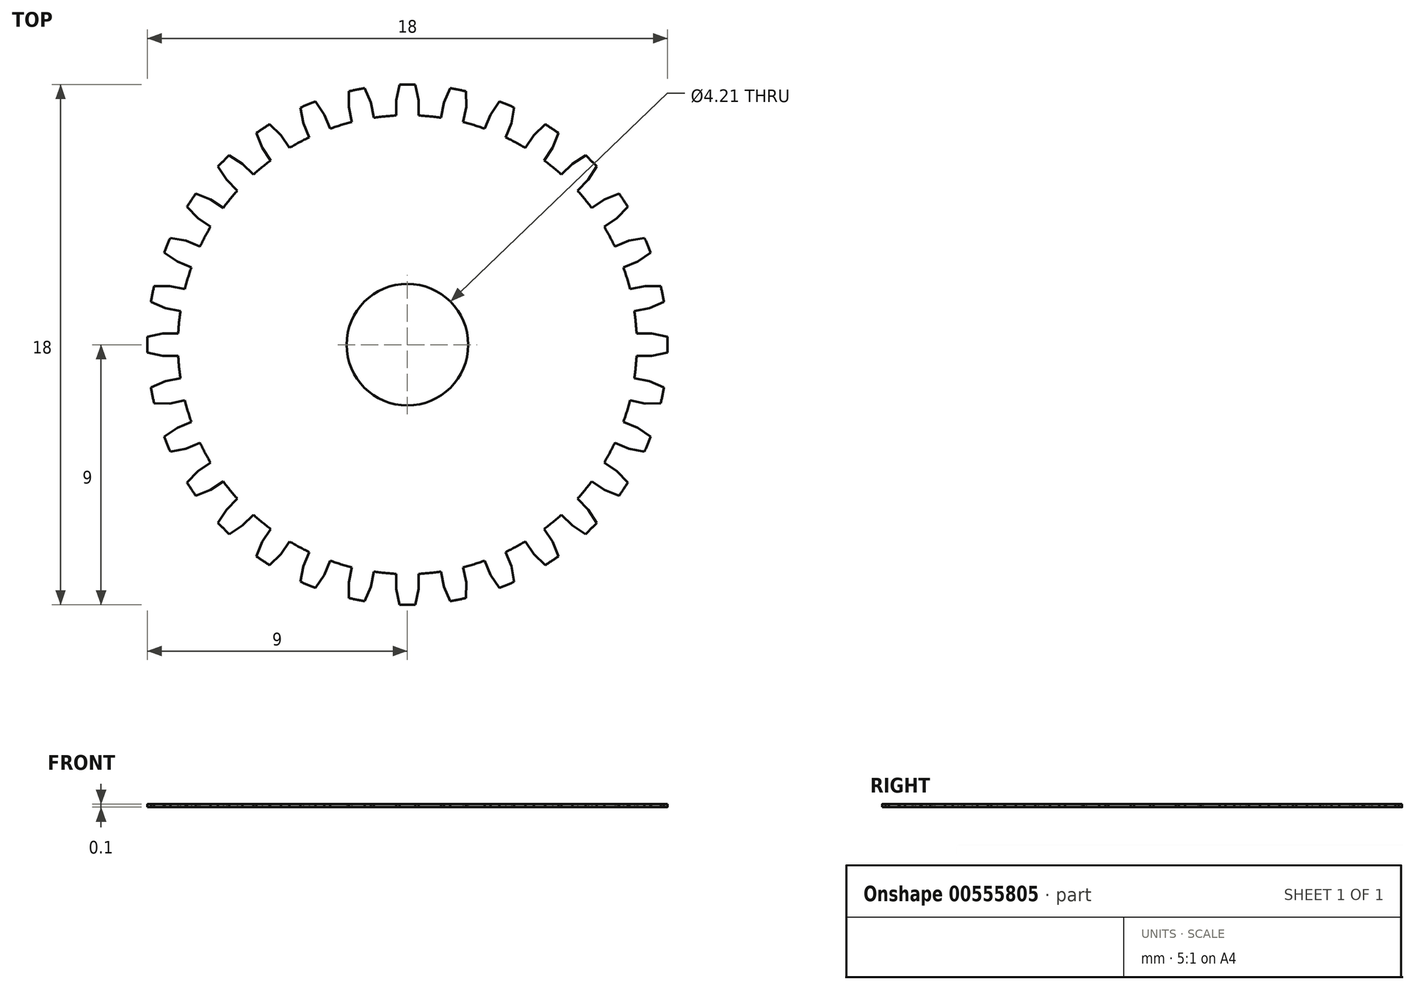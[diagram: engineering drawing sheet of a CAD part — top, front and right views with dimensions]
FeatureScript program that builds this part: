
annotation { "Feature Type Name" : "Feature", "Feature Type Description" : "" }
export const myFeature = defineFeature(function(context is Context, id is Id, definition is map)
    precondition{}
    {
        {
            var Q0;
            Q0=qCreatedBy(makeId("Top.planeOp"),FACE);
            var sketch = newSketch(context, id + "F0", { "sketchPlane" : qUnion([Q0])});
            skCircle(sketch, "E0", {"center": v(0, 0) * mm, "radius": 1.9 * mm});
            skCircle(sketch, "E1.0", {"center": v(0, 0) * mm, "radius": 2.1 * mm});
            skCircle(sketch, "E2", {"center": v(0, 0) * mm, "radius": 8.47 * mm});
            skCircle(sketch, "E3", {"center": v(0, 0) * mm, "radius": 9 * mm});
            skCircle(sketch, "E4", {"center": v(0, 0) * mm, "radius": 7.94 * mm});
            skLineSegment(sketch, "E5", {"start": v(0, 0) * mm, "end": v(0, 9) * mm});
            skLineSegment(sketch, "E6", {"start": v(0, 0) * mm, "end": v(0.88, 8.95) * mm});
            skPoint(sketch, "E7", {"position": v(0.39, 7.93) * mm});
            skPoint(sketch, "E8", {"position": v(0.28, 9) * mm});
            skPoint(sketch, "E9", {"position": v(0.39, 8.46) * mm});
            skArc(sketch, "E10", {"start": v(0.39, 7.93) * mm, "mid": v(0.58, 7.92) * mm, "end": v(0.78, 7.9) * mm});
            skArc(sketch, "E11", {"start": v(0, 9) * mm, "mid": v(0.14, 9) * mm, "end": v(0.28, 9) * mm});
            skLineSegment(sketch, "E12", {"start": v(0.28, 9) * mm, "end": v(0.39, 8.46) * mm});
            skLineSegment(sketch, "E13", {"start": v(0.39, 7.93) * mm, "end": v(0.39, 8.46) * mm});
            skArc(sketch, "E14.MirrorCS", {"start": v(0, 9) * mm, "mid": v(-0.14, 9) * mm, "end": v(-0.28, 9) * mm});
            skPoint(sketch, "E15.MirrorP", {"position": v(-0.39, 8.46) * mm});
            skPoint(sketch, "E16.MirrorP", {"position": v(-0.39, 7.93) * mm});
            skPoint(sketch, "E17.MirrorP", {"position": v(-0.28, 9) * mm});
            skArc(sketch, "E18.MirrorCS", {"start": v(-0.39, 7.93) * mm, "mid": v(-0.58, 7.92) * mm, "end": v(-0.78, 7.9) * mm});
            skLineSegment(sketch, "E19.MirrorCS", {"start": v(-0.39, 7.93) * mm, "end": v(-0.39, 8.46) * mm});
            skLineSegment(sketch, "E20.MirrorCS", {"start": v(-0.28, 9) * mm, "end": v(-0.39, 8.46) * mm});
            skPoint(sketch, "E21.1.0", {"position": v(-2.03, 8.22) * mm});
            skPoint(sketch, "E21.1.1", {"position": v(-2.02, 8.76) * mm});
            skPoint(sketch, "E21.1.2", {"position": v(-1.93, 7.7) * mm});
            skArc(sketch, "E21.1.3", {"start": v(-1.16, 7.85) * mm, "mid": v(-0.97, 7.88) * mm, "end": v(-0.78, 7.9) * mm});
            skLineSegment(sketch, "E21.1.4", {"start": v(-1.48, 8.87) * mm, "end": v(-1.27, 8.37) * mm});
            skLineSegment(sketch, "E21.1.5", {"start": v(-1.16, 7.85) * mm, "end": v(-1.27, 8.37) * mm});
            skArc(sketch, "E21.1.6", {"start": v(-1.93, 7.7) * mm, "mid": v(-2.12, 7.65) * mm, "end": v(-2.3, 7.6) * mm});
            skPoint(sketch, "E21.1.7", {"position": v(-1.27, 8.37) * mm});
            skPoint(sketch, "E21.1.8", {"position": v(-1.48, 8.87) * mm});
            skPoint(sketch, "E21.1.9", {"position": v(-1.16, 7.85) * mm});
            skLineSegment(sketch, "E21.1.10", {"start": v(-1.93, 7.7) * mm, "end": v(-2.03, 8.22) * mm});
            skLineSegment(sketch, "E21.1.11", {"start": v(-2.02, 8.76) * mm, "end": v(-2.03, 8.22) * mm});
            skArc(sketch, "E21.1.12", {"start": v(-1.76, 8.82) * mm, "mid": v(-1.62, 8.85) * mm, "end": v(-1.48, 8.87) * mm});
            skArc(sketch, "E21.1.13", {"start": v(-1.76, 8.82) * mm, "mid": v(-1.9, 8.8) * mm, "end": v(-2.02, 8.76) * mm});
            skPoint(sketch, "E21.2.0", {"position": v(-3.6, 7.66) * mm});
            skPoint(sketch, "E21.2.1", {"position": v(-3.7, 8.2) * mm});
            skPoint(sketch, "E21.2.2", {"position": v(-3.4, 7.18) * mm});
            skArc(sketch, "E21.2.3", {"start": v(-2.67, 7.47) * mm, "mid": v(-2.49, 7.54) * mm, "end": v(-2.3, 7.6) * mm});
            skLineSegment(sketch, "E21.2.4", {"start": v(-3.19, 8.41) * mm, "end": v(-2.88, 7.96) * mm});
            skLineSegment(sketch, "E21.2.5", {"start": v(-2.67, 7.47) * mm, "end": v(-2.88, 7.96) * mm});
            skArc(sketch, "E21.2.6", {"start": v(-3.4, 7.18) * mm, "mid": v(-3.57, 7.09) * mm, "end": v(-3.74, 7) * mm});
            skPoint(sketch, "E21.2.7", {"position": v(-2.88, 7.96) * mm});
            skPoint(sketch, "E21.2.8", {"position": v(-3.19, 8.41) * mm});
            skPoint(sketch, "E21.2.9", {"position": v(-2.67, 7.47) * mm});
            skLineSegment(sketch, "E21.2.10", {"start": v(-3.4, 7.18) * mm, "end": v(-3.6, 7.66) * mm});
            skLineSegment(sketch, "E21.2.11", {"start": v(-3.7, 8.2) * mm, "end": v(-3.6, 7.66) * mm});
            skArc(sketch, "E21.2.12", {"start": v(-3.44, 8.31) * mm, "mid": v(-3.31, 8.36) * mm, "end": v(-3.19, 8.41) * mm});
            skArc(sketch, "E21.2.13", {"start": v(-3.44, 8.31) * mm, "mid": v(-3.57, 8.26) * mm, "end": v(-3.7, 8.2) * mm});
            skPoint(sketch, "E21.3.0", {"position": v(-5.02, 6.82) * mm});
            skPoint(sketch, "E21.3.1", {"position": v(-5.22, 7.32) * mm});
            skPoint(sketch, "E21.3.2", {"position": v(-4.73, 6.38) * mm});
            skArc(sketch, "E21.3.3", {"start": v(-4.08, 6.8) * mm, "mid": v(-3.91, 6.9) * mm, "end": v(-3.74, 7) * mm});
            skLineSegment(sketch, "E21.3.4", {"start": v(-4.77, 7.63) * mm, "end": v(-4.37, 7.25) * mm});
            skLineSegment(sketch, "E21.3.5", {"start": v(-4.08, 6.8) * mm, "end": v(-4.37, 7.25) * mm});
            skArc(sketch, "E21.3.6", {"start": v(-4.73, 6.38) * mm, "mid": v(-4.88, 6.26) * mm, "end": v(-5.04, 6.14) * mm});
            skPoint(sketch, "E21.3.7", {"position": v(-4.37, 7.25) * mm});
            skPoint(sketch, "E21.3.8", {"position": v(-4.77, 7.63) * mm});
            skPoint(sketch, "E21.3.9", {"position": v(-4.08, 6.8) * mm});
            skLineSegment(sketch, "E21.3.10", {"start": v(-4.73, 6.38) * mm, "end": v(-5.02, 6.82) * mm});
            skLineSegment(sketch, "E21.3.11", {"start": v(-5.22, 7.32) * mm, "end": v(-5.02, 6.82) * mm});
            skArc(sketch, "E21.3.12", {"start": v(-5, 7.48) * mm, "mid": v(-4.88, 7.56) * mm, "end": v(-4.77, 7.63) * mm});
            skArc(sketch, "E21.3.13", {"start": v(-5, 7.48) * mm, "mid": v(-5.11, 7.4) * mm, "end": v(-5.22, 7.32) * mm});
            skPoint(sketch, "E21.4.0", {"position": v(-6.26, 5.7) * mm});
            skPoint(sketch, "E21.4.1", {"position": v(-6.55, 6.16) * mm});
            skPoint(sketch, "E21.4.2", {"position": v(-5.88, 5.33) * mm});
            skArc(sketch, "E21.4.3", {"start": v(-5.33, 5.88) * mm, "mid": v(-5.18, 6.01) * mm, "end": v(-5.04, 6.14) * mm});
            skLineSegment(sketch, "E21.4.4", {"start": v(-6.16, 6.55) * mm, "end": v(-5.7, 6.26) * mm});
            skLineSegment(sketch, "E21.4.5", {"start": v(-5.33, 5.88) * mm, "end": v(-5.7, 6.26) * mm});
            skArc(sketch, "E21.4.6", {"start": v(-5.88, 5.33) * mm, "mid": v(-6.01, 5.18) * mm, "end": v(-6.14, 5.04) * mm});
            skPoint(sketch, "E21.4.7", {"position": v(-5.7, 6.26) * mm});
            skPoint(sketch, "E21.4.8", {"position": v(-6.16, 6.55) * mm});
            skPoint(sketch, "E21.4.9", {"position": v(-5.33, 5.88) * mm});
            skLineSegment(sketch, "E21.4.10", {"start": v(-5.88, 5.33) * mm, "end": v(-6.26, 5.7) * mm});
            skLineSegment(sketch, "E21.4.11", {"start": v(-6.55, 6.16) * mm, "end": v(-6.26, 5.7) * mm});
            skArc(sketch, "E21.4.12", {"start": v(-6.36, 6.36) * mm, "mid": v(-6.26, 6.46) * mm, "end": v(-6.16, 6.55) * mm});
            skArc(sketch, "E21.4.13", {"start": v(-6.36, 6.36) * mm, "mid": v(-6.46, 6.26) * mm, "end": v(-6.55, 6.16) * mm});
            skPoint(sketch, "E21.5.0", {"position": v(-7.25, 4.37) * mm});
            skPoint(sketch, "E21.5.1", {"position": v(-7.63, 4.77) * mm});
            skPoint(sketch, "E21.5.2", {"position": v(-6.8, 4.08) * mm});
            skArc(sketch, "E21.5.3", {"start": v(-6.38, 4.73) * mm, "mid": v(-6.26, 4.88) * mm, "end": v(-6.14, 5.04) * mm});
            skLineSegment(sketch, "E21.5.4", {"start": v(-7.32, 5.22) * mm, "end": v(-6.82, 5.02) * mm});
            skLineSegment(sketch, "E21.5.5", {"start": v(-6.38, 4.73) * mm, "end": v(-6.82, 5.02) * mm});
            skArc(sketch, "E21.5.6", {"start": v(-6.8, 4.08) * mm, "mid": v(-6.9, 3.91) * mm, "end": v(-7, 3.74) * mm});
            skPoint(sketch, "E21.5.7", {"position": v(-6.82, 5.02) * mm});
            skPoint(sketch, "E21.5.8", {"position": v(-7.32, 5.22) * mm});
            skPoint(sketch, "E21.5.9", {"position": v(-6.38, 4.73) * mm});
            skLineSegment(sketch, "E21.5.10", {"start": v(-6.8, 4.08) * mm, "end": v(-7.25, 4.37) * mm});
            skLineSegment(sketch, "E21.5.11", {"start": v(-7.63, 4.77) * mm, "end": v(-7.25, 4.37) * mm});
            skArc(sketch, "E21.5.12", {"start": v(-7.48, 5) * mm, "mid": v(-7.4, 5.11) * mm, "end": v(-7.32, 5.22) * mm});
            skArc(sketch, "E21.5.13", {"start": v(-7.48, 5) * mm, "mid": v(-7.56, 4.88) * mm, "end": v(-7.63, 4.77) * mm});
            skPoint(sketch, "E21.6.0", {"position": v(-7.96, 2.88) * mm});
            skPoint(sketch, "E21.6.1", {"position": v(-8.41, 3.19) * mm});
            skPoint(sketch, "E21.6.2", {"position": v(-7.47, 2.67) * mm});
            skArc(sketch, "E21.6.3", {"start": v(-7.18, 3.4) * mm, "mid": v(-7.09, 3.57) * mm, "end": v(-7, 3.74) * mm});
            skLineSegment(sketch, "E21.6.4", {"start": v(-8.2, 3.7) * mm, "end": v(-7.66, 3.6) * mm});
            skLineSegment(sketch, "E21.6.5", {"start": v(-7.18, 3.4) * mm, "end": v(-7.66, 3.6) * mm});
            skArc(sketch, "E21.6.6", {"start": v(-7.47, 2.67) * mm, "mid": v(-7.54, 2.49) * mm, "end": v(-7.6, 2.3) * mm});
            skPoint(sketch, "E21.6.7", {"position": v(-7.66, 3.6) * mm});
            skPoint(sketch, "E21.6.8", {"position": v(-8.2, 3.7) * mm});
            skPoint(sketch, "E21.6.9", {"position": v(-7.18, 3.4) * mm});
            skLineSegment(sketch, "E21.6.10", {"start": v(-7.47, 2.67) * mm, "end": v(-7.96, 2.88) * mm});
            skLineSegment(sketch, "E21.6.11", {"start": v(-8.41, 3.19) * mm, "end": v(-7.96, 2.88) * mm});
            skArc(sketch, "E21.6.12", {"start": v(-8.31, 3.44) * mm, "mid": v(-8.26, 3.57) * mm, "end": v(-8.2, 3.7) * mm});
            skArc(sketch, "E21.6.13", {"start": v(-8.31, 3.44) * mm, "mid": v(-8.36, 3.31) * mm, "end": v(-8.41, 3.19) * mm});
            skPoint(sketch, "E21.7.0", {"position": v(-8.37, 1.27) * mm});
            skPoint(sketch, "E21.7.1", {"position": v(-8.87, 1.48) * mm});
            skPoint(sketch, "E21.7.2", {"position": v(-7.85, 1.16) * mm});
            skArc(sketch, "E21.7.3", {"start": v(-7.7, 1.93) * mm, "mid": v(-7.65, 2.12) * mm, "end": v(-7.6, 2.3) * mm});
            skLineSegment(sketch, "E21.7.4", {"start": v(-8.76, 2.02) * mm, "end": v(-8.22, 2.03) * mm});
            skLineSegment(sketch, "E21.7.5", {"start": v(-7.7, 1.93) * mm, "end": v(-8.22, 2.03) * mm});
            skArc(sketch, "E21.7.6", {"start": v(-7.85, 1.16) * mm, "mid": v(-7.88, 0.97) * mm, "end": v(-7.9, 0.78) * mm});
            skPoint(sketch, "E21.7.7", {"position": v(-8.22, 2.03) * mm});
            skPoint(sketch, "E21.7.8", {"position": v(-8.76, 2.02) * mm});
            skPoint(sketch, "E21.7.9", {"position": v(-7.7, 1.93) * mm});
            skLineSegment(sketch, "E21.7.10", {"start": v(-7.85, 1.16) * mm, "end": v(-8.37, 1.27) * mm});
            skLineSegment(sketch, "E21.7.11", {"start": v(-8.87, 1.48) * mm, "end": v(-8.37, 1.27) * mm});
            skArc(sketch, "E21.7.12", {"start": v(-8.82, 1.76) * mm, "mid": v(-8.8, 1.9) * mm, "end": v(-8.76, 2.02) * mm});
            skArc(sketch, "E21.7.13", {"start": v(-8.82, 1.76) * mm, "mid": v(-8.85, 1.62) * mm, "end": v(-8.87, 1.48) * mm});
            skPoint(sketch, "E21.8.0", {"position": v(-8.46, -0.39) * mm});
            skPoint(sketch, "E21.8.1", {"position": v(-9, -0.28) * mm});
            skPoint(sketch, "E21.8.2", {"position": v(-7.93, -0.39) * mm});
            skArc(sketch, "E21.8.3", {"start": v(-7.93, 0.39) * mm, "mid": v(-7.92, 0.58) * mm, "end": v(-7.9, 0.78) * mm});
            skLineSegment(sketch, "E21.8.4", {"start": v(-9, 0.28) * mm, "end": v(-8.46, 0.39) * mm});
            skLineSegment(sketch, "E21.8.5", {"start": v(-7.93, 0.39) * mm, "end": v(-8.46, 0.39) * mm});
            skArc(sketch, "E21.8.6", {"start": v(-7.93, -0.39) * mm, "mid": v(-7.92, -0.58) * mm, "end": v(-7.9, -0.78) * mm});
            skPoint(sketch, "E21.8.7", {"position": v(-8.46, 0.39) * mm});
            skPoint(sketch, "E21.8.8", {"position": v(-9, 0.28) * mm});
            skPoint(sketch, "E21.8.9", {"position": v(-7.93, 0.39) * mm});
            skLineSegment(sketch, "E21.8.10", {"start": v(-7.93, -0.39) * mm, "end": v(-8.46, -0.39) * mm});
            skLineSegment(sketch, "E21.8.11", {"start": v(-9, -0.28) * mm, "end": v(-8.46, -0.39) * mm});
            skArc(sketch, "E21.8.12", {"start": v(-9, 0) * mm, "mid": v(-9, 0.14) * mm, "end": v(-9, 0.28) * mm});
            skArc(sketch, "E21.8.13", {"start": v(-9, 0) * mm, "mid": v(-9, -0.14) * mm, "end": v(-9, -0.28) * mm});
            skPoint(sketch, "E21.9.0", {"position": v(-8.22, -2.03) * mm});
            skPoint(sketch, "E21.9.1", {"position": v(-8.76, -2.02) * mm});
            skPoint(sketch, "E21.9.2", {"position": v(-7.7, -1.93) * mm});
            skArc(sketch, "E21.9.3", {"start": v(-7.85, -1.16) * mm, "mid": v(-7.88, -0.97) * mm, "end": v(-7.9, -0.78) * mm});
            skLineSegment(sketch, "E21.9.4", {"start": v(-8.87, -1.48) * mm, "end": v(-8.37, -1.27) * mm});
            skLineSegment(sketch, "E21.9.5", {"start": v(-7.85, -1.16) * mm, "end": v(-8.37, -1.27) * mm});
            skArc(sketch, "E21.9.6", {"start": v(-7.7, -1.93) * mm, "mid": v(-7.65, -2.12) * mm, "end": v(-7.6, -2.3) * mm});
            skPoint(sketch, "E21.9.7", {"position": v(-8.37, -1.27) * mm});
            skPoint(sketch, "E21.9.8", {"position": v(-8.87, -1.48) * mm});
            skPoint(sketch, "E21.9.9", {"position": v(-7.85, -1.16) * mm});
            skLineSegment(sketch, "E21.9.10", {"start": v(-7.7, -1.93) * mm, "end": v(-8.22, -2.03) * mm});
            skLineSegment(sketch, "E21.9.11", {"start": v(-8.76, -2.02) * mm, "end": v(-8.22, -2.03) * mm});
            skArc(sketch, "E21.9.12", {"start": v(-8.82, -1.76) * mm, "mid": v(-8.85, -1.62) * mm, "end": v(-8.87, -1.48) * mm});
            skArc(sketch, "E21.9.13", {"start": v(-8.82, -1.76) * mm, "mid": v(-8.8, -1.9) * mm, "end": v(-8.76, -2.02) * mm});
            skPoint(sketch, "E21.10.0", {"position": v(-7.66, -3.6) * mm});
            skPoint(sketch, "E21.10.1", {"position": v(-8.2, -3.7) * mm});
            skPoint(sketch, "E21.10.2", {"position": v(-7.18, -3.4) * mm});
            skArc(sketch, "E21.10.3", {"start": v(-7.47, -2.67) * mm, "mid": v(-7.54, -2.49) * mm, "end": v(-7.6, -2.3) * mm});
            skLineSegment(sketch, "E21.10.4", {"start": v(-8.41, -3.19) * mm, "end": v(-7.96, -2.88) * mm});
            skLineSegment(sketch, "E21.10.5", {"start": v(-7.47, -2.67) * mm, "end": v(-7.96, -2.88) * mm});
            skArc(sketch, "E21.10.6", {"start": v(-7.18, -3.4) * mm, "mid": v(-7.09, -3.57) * mm, "end": v(-7, -3.74) * mm});
            skPoint(sketch, "E21.10.7", {"position": v(-7.96, -2.88) * mm});
            skPoint(sketch, "E21.10.8", {"position": v(-8.41, -3.19) * mm});
            skPoint(sketch, "E21.10.9", {"position": v(-7.47, -2.67) * mm});
            skLineSegment(sketch, "E21.10.10", {"start": v(-7.18, -3.4) * mm, "end": v(-7.66, -3.6) * mm});
            skLineSegment(sketch, "E21.10.11", {"start": v(-8.2, -3.7) * mm, "end": v(-7.66, -3.6) * mm});
            skArc(sketch, "E21.10.12", {"start": v(-8.31, -3.44) * mm, "mid": v(-8.36, -3.31) * mm, "end": v(-8.41, -3.19) * mm});
            skArc(sketch, "E21.10.13", {"start": v(-8.31, -3.44) * mm, "mid": v(-8.26, -3.57) * mm, "end": v(-8.2, -3.7) * mm});
            skPoint(sketch, "E21.11.0", {"position": v(-6.82, -5.02) * mm});
            skPoint(sketch, "E21.11.1", {"position": v(-7.32, -5.22) * mm});
            skPoint(sketch, "E21.11.2", {"position": v(-6.38, -4.73) * mm});
            skArc(sketch, "E21.11.3", {"start": v(-6.8, -4.08) * mm, "mid": v(-6.9, -3.91) * mm, "end": v(-7, -3.74) * mm});
            skLineSegment(sketch, "E21.11.4", {"start": v(-7.63, -4.77) * mm, "end": v(-7.25, -4.37) * mm});
            skLineSegment(sketch, "E21.11.5", {"start": v(-6.8, -4.08) * mm, "end": v(-7.25, -4.37) * mm});
            skArc(sketch, "E21.11.6", {"start": v(-6.38, -4.73) * mm, "mid": v(-6.26, -4.88) * mm, "end": v(-6.14, -5.04) * mm});
            skPoint(sketch, "E21.11.7", {"position": v(-7.25, -4.37) * mm});
            skPoint(sketch, "E21.11.8", {"position": v(-7.63, -4.77) * mm});
            skPoint(sketch, "E21.11.9", {"position": v(-6.8, -4.08) * mm});
            skLineSegment(sketch, "E21.11.10", {"start": v(-6.38, -4.73) * mm, "end": v(-6.82, -5.02) * mm});
            skLineSegment(sketch, "E21.11.11", {"start": v(-7.32, -5.22) * mm, "end": v(-6.82, -5.02) * mm});
            skArc(sketch, "E21.11.12", {"start": v(-7.48, -5) * mm, "mid": v(-7.56, -4.88) * mm, "end": v(-7.63, -4.77) * mm});
            skArc(sketch, "E21.11.13", {"start": v(-7.48, -5) * mm, "mid": v(-7.4, -5.11) * mm, "end": v(-7.32, -5.22) * mm});
            skPoint(sketch, "E21.12.0", {"position": v(-5.7, -6.26) * mm});
            skPoint(sketch, "E21.12.1", {"position": v(-6.16, -6.55) * mm});
            skPoint(sketch, "E21.12.2", {"position": v(-5.33, -5.88) * mm});
            skArc(sketch, "E21.12.3", {"start": v(-5.88, -5.33) * mm, "mid": v(-6.01, -5.18) * mm, "end": v(-6.14, -5.04) * mm});
            skLineSegment(sketch, "E21.12.4", {"start": v(-6.55, -6.16) * mm, "end": v(-6.26, -5.7) * mm});
            skLineSegment(sketch, "E21.12.5", {"start": v(-5.88, -5.33) * mm, "end": v(-6.26, -5.7) * mm});
            skArc(sketch, "E21.12.6", {"start": v(-5.33, -5.88) * mm, "mid": v(-5.18, -6.01) * mm, "end": v(-5.04, -6.14) * mm});
            skPoint(sketch, "E21.12.7", {"position": v(-6.26, -5.7) * mm});
            skPoint(sketch, "E21.12.8", {"position": v(-6.55, -6.16) * mm});
            skPoint(sketch, "E21.12.9", {"position": v(-5.88, -5.33) * mm});
            skLineSegment(sketch, "E21.12.10", {"start": v(-5.33, -5.88) * mm, "end": v(-5.7, -6.26) * mm});
            skLineSegment(sketch, "E21.12.11", {"start": v(-6.16, -6.55) * mm, "end": v(-5.7, -6.26) * mm});
            skArc(sketch, "E21.12.12", {"start": v(-6.36, -6.36) * mm, "mid": v(-6.46, -6.26) * mm, "end": v(-6.55, -6.16) * mm});
            skArc(sketch, "E21.12.13", {"start": v(-6.36, -6.36) * mm, "mid": v(-6.26, -6.46) * mm, "end": v(-6.16, -6.55) * mm});
            skPoint(sketch, "E21.13.0", {"position": v(-4.37, -7.25) * mm});
            skPoint(sketch, "E21.13.1", {"position": v(-4.77, -7.63) * mm});
            skPoint(sketch, "E21.13.2", {"position": v(-4.08, -6.8) * mm});
            skArc(sketch, "E21.13.3", {"start": v(-4.73, -6.38) * mm, "mid": v(-4.88, -6.26) * mm, "end": v(-5.04, -6.14) * mm});
            skLineSegment(sketch, "E21.13.4", {"start": v(-5.22, -7.32) * mm, "end": v(-5.02, -6.82) * mm});
            skLineSegment(sketch, "E21.13.5", {"start": v(-4.73, -6.38) * mm, "end": v(-5.02, -6.82) * mm});
            skArc(sketch, "E21.13.6", {"start": v(-4.08, -6.8) * mm, "mid": v(-3.91, -6.9) * mm, "end": v(-3.74, -7) * mm});
            skPoint(sketch, "E21.13.7", {"position": v(-5.02, -6.82) * mm});
            skPoint(sketch, "E21.13.8", {"position": v(-5.22, -7.32) * mm});
            skPoint(sketch, "E21.13.9", {"position": v(-4.73, -6.38) * mm});
            skLineSegment(sketch, "E21.13.10", {"start": v(-4.08, -6.8) * mm, "end": v(-4.37, -7.25) * mm});
            skLineSegment(sketch, "E21.13.11", {"start": v(-4.77, -7.63) * mm, "end": v(-4.37, -7.25) * mm});
            skArc(sketch, "E21.13.12", {"start": v(-5, -7.48) * mm, "mid": v(-5.11, -7.4) * mm, "end": v(-5.22, -7.32) * mm});
            skArc(sketch, "E21.13.13", {"start": v(-5, -7.48) * mm, "mid": v(-4.88, -7.56) * mm, "end": v(-4.77, -7.63) * mm});
            skPoint(sketch, "E21.14.0", {"position": v(-2.88, -7.96) * mm});
            skPoint(sketch, "E21.14.1", {"position": v(-3.19, -8.41) * mm});
            skPoint(sketch, "E21.14.2", {"position": v(-2.67, -7.47) * mm});
            skArc(sketch, "E21.14.3", {"start": v(-3.4, -7.18) * mm, "mid": v(-3.57, -7.09) * mm, "end": v(-3.74, -7) * mm});
            skLineSegment(sketch, "E21.14.4", {"start": v(-3.7, -8.2) * mm, "end": v(-3.6, -7.66) * mm});
            skLineSegment(sketch, "E21.14.5", {"start": v(-3.4, -7.18) * mm, "end": v(-3.6, -7.66) * mm});
            skArc(sketch, "E21.14.6", {"start": v(-2.67, -7.47) * mm, "mid": v(-2.49, -7.54) * mm, "end": v(-2.3, -7.6) * mm});
            skPoint(sketch, "E21.14.7", {"position": v(-3.6, -7.66) * mm});
            skPoint(sketch, "E21.14.8", {"position": v(-3.7, -8.2) * mm});
            skPoint(sketch, "E21.14.9", {"position": v(-3.4, -7.18) * mm});
            skLineSegment(sketch, "E21.14.10", {"start": v(-2.67, -7.47) * mm, "end": v(-2.88, -7.96) * mm});
            skLineSegment(sketch, "E21.14.11", {"start": v(-3.19, -8.41) * mm, "end": v(-2.88, -7.96) * mm});
            skArc(sketch, "E21.14.12", {"start": v(-3.44, -8.31) * mm, "mid": v(-3.57, -8.26) * mm, "end": v(-3.7, -8.2) * mm});
            skArc(sketch, "E21.14.13", {"start": v(-3.44, -8.31) * mm, "mid": v(-3.31, -8.36) * mm, "end": v(-3.19, -8.41) * mm});
            skPoint(sketch, "E21.15.0", {"position": v(-1.27, -8.37) * mm});
            skPoint(sketch, "E21.15.1", {"position": v(-1.48, -8.87) * mm});
            skPoint(sketch, "E21.15.2", {"position": v(-1.16, -7.85) * mm});
            skArc(sketch, "E21.15.3", {"start": v(-1.93, -7.7) * mm, "mid": v(-2.12, -7.65) * mm, "end": v(-2.3, -7.6) * mm});
            skLineSegment(sketch, "E21.15.4", {"start": v(-2.02, -8.76) * mm, "end": v(-2.03, -8.22) * mm});
            skLineSegment(sketch, "E21.15.5", {"start": v(-1.93, -7.7) * mm, "end": v(-2.03, -8.22) * mm});
            skArc(sketch, "E21.15.6", {"start": v(-1.16, -7.85) * mm, "mid": v(-0.97, -7.88) * mm, "end": v(-0.78, -7.9) * mm});
            skPoint(sketch, "E21.15.7", {"position": v(-2.03, -8.22) * mm});
            skPoint(sketch, "E21.15.8", {"position": v(-2.02, -8.76) * mm});
            skPoint(sketch, "E21.15.9", {"position": v(-1.93, -7.7) * mm});
            skLineSegment(sketch, "E21.15.10", {"start": v(-1.16, -7.85) * mm, "end": v(-1.27, -8.37) * mm});
            skLineSegment(sketch, "E21.15.11", {"start": v(-1.48, -8.87) * mm, "end": v(-1.27, -8.37) * mm});
            skArc(sketch, "E21.15.12", {"start": v(-1.76, -8.82) * mm, "mid": v(-1.9, -8.8) * mm, "end": v(-2.02, -8.76) * mm});
            skArc(sketch, "E21.15.13", {"start": v(-1.76, -8.82) * mm, "mid": v(-1.62, -8.85) * mm, "end": v(-1.48, -8.87) * mm});
            skPoint(sketch, "E21.16.0", {"position": v(0.39, -8.46) * mm});
            skPoint(sketch, "E21.16.1", {"position": v(0.28, -9) * mm});
            skPoint(sketch, "E21.16.2", {"position": v(0.39, -7.93) * mm});
            skArc(sketch, "E21.16.3", {"start": v(-0.39, -7.93) * mm, "mid": v(-0.58, -7.92) * mm, "end": v(-0.78, -7.9) * mm});
            skLineSegment(sketch, "E21.16.4", {"start": v(-0.28, -9) * mm, "end": v(-0.39, -8.46) * mm});
            skLineSegment(sketch, "E21.16.5", {"start": v(-0.39, -7.93) * mm, "end": v(-0.39, -8.46) * mm});
            skArc(sketch, "E21.16.6", {"start": v(0.39, -7.93) * mm, "mid": v(0.58, -7.92) * mm, "end": v(0.78, -7.9) * mm});
            skPoint(sketch, "E21.16.7", {"position": v(-0.39, -8.46) * mm});
            skPoint(sketch, "E21.16.8", {"position": v(-0.28, -9) * mm});
            skPoint(sketch, "E21.16.9", {"position": v(-0.39, -7.93) * mm});
            skLineSegment(sketch, "E21.16.10", {"start": v(0.39, -7.93) * mm, "end": v(0.39, -8.46) * mm});
            skLineSegment(sketch, "E21.16.11", {"start": v(0.28, -9) * mm, "end": v(0.39, -8.46) * mm});
            skArc(sketch, "E21.16.12", {"start": v(0, -9) * mm, "mid": v(-0.14, -9) * mm, "end": v(-0.28, -9) * mm});
            skArc(sketch, "E21.16.13", {"start": v(0, -9) * mm, "mid": v(0.14, -9) * mm, "end": v(0.28, -9) * mm});
            skPoint(sketch, "E21.17.0", {"position": v(2.03, -8.22) * mm});
            skPoint(sketch, "E21.17.1", {"position": v(2.02, -8.76) * mm});
            skPoint(sketch, "E21.17.2", {"position": v(1.93, -7.7) * mm});
            skArc(sketch, "E21.17.3", {"start": v(1.16, -7.85) * mm, "mid": v(0.97, -7.88) * mm, "end": v(0.78, -7.9) * mm});
            skLineSegment(sketch, "E21.17.4", {"start": v(1.48, -8.87) * mm, "end": v(1.27, -8.37) * mm});
            skLineSegment(sketch, "E21.17.5", {"start": v(1.16, -7.85) * mm, "end": v(1.27, -8.37) * mm});
            skArc(sketch, "E21.17.6", {"start": v(1.93, -7.7) * mm, "mid": v(2.12, -7.65) * mm, "end": v(2.3, -7.6) * mm});
            skPoint(sketch, "E21.17.7", {"position": v(1.27, -8.37) * mm});
            skPoint(sketch, "E21.17.8", {"position": v(1.48, -8.87) * mm});
            skPoint(sketch, "E21.17.9", {"position": v(1.16, -7.85) * mm});
            skLineSegment(sketch, "E21.17.10", {"start": v(1.93, -7.7) * mm, "end": v(2.03, -8.22) * mm});
            skLineSegment(sketch, "E21.17.11", {"start": v(2.02, -8.76) * mm, "end": v(2.03, -8.22) * mm});
            skArc(sketch, "E21.17.12", {"start": v(1.76, -8.82) * mm, "mid": v(1.62, -8.85) * mm, "end": v(1.48, -8.87) * mm});
            skArc(sketch, "E21.17.13", {"start": v(1.76, -8.82) * mm, "mid": v(1.9, -8.8) * mm, "end": v(2.02, -8.76) * mm});
            skPoint(sketch, "E21.18.0", {"position": v(3.6, -7.66) * mm});
            skPoint(sketch, "E21.18.1", {"position": v(3.7, -8.2) * mm});
            skPoint(sketch, "E21.18.2", {"position": v(3.4, -7.18) * mm});
            skArc(sketch, "E21.18.3", {"start": v(2.67, -7.47) * mm, "mid": v(2.49, -7.54) * mm, "end": v(2.3, -7.6) * mm});
            skLineSegment(sketch, "E21.18.4", {"start": v(3.19, -8.41) * mm, "end": v(2.88, -7.96) * mm});
            skLineSegment(sketch, "E21.18.5", {"start": v(2.67, -7.47) * mm, "end": v(2.88, -7.96) * mm});
            skArc(sketch, "E21.18.6", {"start": v(3.4, -7.18) * mm, "mid": v(3.57, -7.09) * mm, "end": v(3.74, -7) * mm});
            skPoint(sketch, "E21.18.7", {"position": v(2.88, -7.96) * mm});
            skPoint(sketch, "E21.18.8", {"position": v(3.19, -8.41) * mm});
            skPoint(sketch, "E21.18.9", {"position": v(2.67, -7.47) * mm});
            skLineSegment(sketch, "E21.18.10", {"start": v(3.4, -7.18) * mm, "end": v(3.6, -7.66) * mm});
            skLineSegment(sketch, "E21.18.11", {"start": v(3.7, -8.2) * mm, "end": v(3.6, -7.66) * mm});
            skArc(sketch, "E21.18.12", {"start": v(3.44, -8.31) * mm, "mid": v(3.31, -8.36) * mm, "end": v(3.19, -8.41) * mm});
            skArc(sketch, "E21.18.13", {"start": v(3.44, -8.31) * mm, "mid": v(3.57, -8.26) * mm, "end": v(3.7, -8.2) * mm});
            skPoint(sketch, "E21.19.0", {"position": v(5.02, -6.82) * mm});
            skPoint(sketch, "E21.19.1", {"position": v(5.22, -7.32) * mm});
            skPoint(sketch, "E21.19.2", {"position": v(4.73, -6.38) * mm});
            skArc(sketch, "E21.19.3", {"start": v(4.08, -6.8) * mm, "mid": v(3.91, -6.9) * mm, "end": v(3.74, -7) * mm});
            skLineSegment(sketch, "E21.19.4", {"start": v(4.77, -7.63) * mm, "end": v(4.37, -7.25) * mm});
            skLineSegment(sketch, "E21.19.5", {"start": v(4.08, -6.8) * mm, "end": v(4.37, -7.25) * mm});
            skArc(sketch, "E21.19.6", {"start": v(4.73, -6.38) * mm, "mid": v(4.88, -6.26) * mm, "end": v(5.04, -6.14) * mm});
            skPoint(sketch, "E21.19.7", {"position": v(4.37, -7.25) * mm});
            skPoint(sketch, "E21.19.8", {"position": v(4.77, -7.63) * mm});
            skPoint(sketch, "E21.19.9", {"position": v(4.08, -6.8) * mm});
            skLineSegment(sketch, "E21.19.10", {"start": v(4.73, -6.38) * mm, "end": v(5.02, -6.82) * mm});
            skLineSegment(sketch, "E21.19.11", {"start": v(5.22, -7.32) * mm, "end": v(5.02, -6.82) * mm});
            skArc(sketch, "E21.19.12", {"start": v(5, -7.48) * mm, "mid": v(4.88, -7.56) * mm, "end": v(4.77, -7.63) * mm});
            skArc(sketch, "E21.19.13", {"start": v(5, -7.48) * mm, "mid": v(5.11, -7.4) * mm, "end": v(5.22, -7.32) * mm});
            skPoint(sketch, "E21.20.0", {"position": v(6.26, -5.7) * mm});
            skPoint(sketch, "E21.20.1", {"position": v(6.55, -6.16) * mm});
            skPoint(sketch, "E21.20.2", {"position": v(5.88, -5.33) * mm});
            skArc(sketch, "E21.20.3", {"start": v(5.33, -5.88) * mm, "mid": v(5.18, -6.01) * mm, "end": v(5.04, -6.14) * mm});
            skLineSegment(sketch, "E21.20.4", {"start": v(6.16, -6.55) * mm, "end": v(5.7, -6.26) * mm});
            skLineSegment(sketch, "E21.20.5", {"start": v(5.33, -5.88) * mm, "end": v(5.7, -6.26) * mm});
            skArc(sketch, "E21.20.6", {"start": v(5.88, -5.33) * mm, "mid": v(6.01, -5.18) * mm, "end": v(6.14, -5.04) * mm});
            skPoint(sketch, "E21.20.7", {"position": v(5.7, -6.26) * mm});
            skPoint(sketch, "E21.20.8", {"position": v(6.16, -6.55) * mm});
            skPoint(sketch, "E21.20.9", {"position": v(5.33, -5.88) * mm});
            skLineSegment(sketch, "E21.20.10", {"start": v(5.88, -5.33) * mm, "end": v(6.26, -5.7) * mm});
            skLineSegment(sketch, "E21.20.11", {"start": v(6.55, -6.16) * mm, "end": v(6.26, -5.7) * mm});
            skArc(sketch, "E21.20.12", {"start": v(6.36, -6.36) * mm, "mid": v(6.26, -6.46) * mm, "end": v(6.16, -6.55) * mm});
            skArc(sketch, "E21.20.13", {"start": v(6.36, -6.36) * mm, "mid": v(6.46, -6.26) * mm, "end": v(6.55, -6.16) * mm});
            skPoint(sketch, "E21.21.0", {"position": v(7.25, -4.37) * mm});
            skPoint(sketch, "E21.21.1", {"position": v(7.63, -4.77) * mm});
            skPoint(sketch, "E21.21.2", {"position": v(6.8, -4.08) * mm});
            skArc(sketch, "E21.21.3", {"start": v(6.38, -4.73) * mm, "mid": v(6.26, -4.88) * mm, "end": v(6.14, -5.04) * mm});
            skLineSegment(sketch, "E21.21.4", {"start": v(7.32, -5.22) * mm, "end": v(6.82, -5.02) * mm});
            skLineSegment(sketch, "E21.21.5", {"start": v(6.38, -4.73) * mm, "end": v(6.82, -5.02) * mm});
            skArc(sketch, "E21.21.6", {"start": v(6.8, -4.08) * mm, "mid": v(6.9, -3.91) * mm, "end": v(7, -3.74) * mm});
            skPoint(sketch, "E21.21.7", {"position": v(6.82, -5.02) * mm});
            skPoint(sketch, "E21.21.8", {"position": v(7.32, -5.22) * mm});
            skPoint(sketch, "E21.21.9", {"position": v(6.38, -4.73) * mm});
            skLineSegment(sketch, "E21.21.10", {"start": v(6.8, -4.08) * mm, "end": v(7.25, -4.37) * mm});
            skLineSegment(sketch, "E21.21.11", {"start": v(7.63, -4.77) * mm, "end": v(7.25, -4.37) * mm});
            skArc(sketch, "E21.21.12", {"start": v(7.48, -5) * mm, "mid": v(7.4, -5.11) * mm, "end": v(7.32, -5.22) * mm});
            skArc(sketch, "E21.21.13", {"start": v(7.48, -5) * mm, "mid": v(7.56, -4.88) * mm, "end": v(7.63, -4.77) * mm});
            skPoint(sketch, "E21.22.0", {"position": v(7.96, -2.88) * mm});
            skPoint(sketch, "E21.22.1", {"position": v(8.41, -3.19) * mm});
            skPoint(sketch, "E21.22.2", {"position": v(7.47, -2.67) * mm});
            skArc(sketch, "E21.22.3", {"start": v(7.18, -3.4) * mm, "mid": v(7.09, -3.57) * mm, "end": v(7, -3.74) * mm});
            skLineSegment(sketch, "E21.22.4", {"start": v(8.2, -3.7) * mm, "end": v(7.66, -3.6) * mm});
            skLineSegment(sketch, "E21.22.5", {"start": v(7.18, -3.4) * mm, "end": v(7.66, -3.6) * mm});
            skArc(sketch, "E21.22.6", {"start": v(7.47, -2.67) * mm, "mid": v(7.54, -2.49) * mm, "end": v(7.6, -2.3) * mm});
            skPoint(sketch, "E21.22.7", {"position": v(7.66, -3.6) * mm});
            skPoint(sketch, "E21.22.8", {"position": v(8.2, -3.7) * mm});
            skPoint(sketch, "E21.22.9", {"position": v(7.18, -3.4) * mm});
            skLineSegment(sketch, "E21.22.10", {"start": v(7.47, -2.67) * mm, "end": v(7.96, -2.88) * mm});
            skLineSegment(sketch, "E21.22.11", {"start": v(8.41, -3.19) * mm, "end": v(7.96, -2.88) * mm});
            skArc(sketch, "E21.22.12", {"start": v(8.31, -3.44) * mm, "mid": v(8.26, -3.57) * mm, "end": v(8.2, -3.7) * mm});
            skArc(sketch, "E21.22.13", {"start": v(8.31, -3.44) * mm, "mid": v(8.36, -3.31) * mm, "end": v(8.41, -3.19) * mm});
            skPoint(sketch, "E21.23.0", {"position": v(8.37, -1.27) * mm});
            skPoint(sketch, "E21.23.1", {"position": v(8.87, -1.48) * mm});
            skPoint(sketch, "E21.23.2", {"position": v(7.85, -1.16) * mm});
            skArc(sketch, "E21.23.3", {"start": v(7.7, -1.93) * mm, "mid": v(7.65, -2.12) * mm, "end": v(7.6, -2.3) * mm});
            skLineSegment(sketch, "E21.23.4", {"start": v(8.76, -2.02) * mm, "end": v(8.22, -2.03) * mm});
            skLineSegment(sketch, "E21.23.5", {"start": v(7.7, -1.93) * mm, "end": v(8.22, -2.03) * mm});
            skArc(sketch, "E21.23.6", {"start": v(7.85, -1.16) * mm, "mid": v(7.88, -0.97) * mm, "end": v(7.9, -0.78) * mm});
            skPoint(sketch, "E21.23.7", {"position": v(8.22, -2.03) * mm});
            skPoint(sketch, "E21.23.8", {"position": v(8.76, -2.02) * mm});
            skPoint(sketch, "E21.23.9", {"position": v(7.7, -1.93) * mm});
            skLineSegment(sketch, "E21.23.10", {"start": v(7.85, -1.16) * mm, "end": v(8.37, -1.27) * mm});
            skLineSegment(sketch, "E21.23.11", {"start": v(8.87, -1.48) * mm, "end": v(8.37, -1.27) * mm});
            skArc(sketch, "E21.23.12", {"start": v(8.82, -1.76) * mm, "mid": v(8.8, -1.9) * mm, "end": v(8.76, -2.02) * mm});
            skArc(sketch, "E21.23.13", {"start": v(8.82, -1.76) * mm, "mid": v(8.85, -1.62) * mm, "end": v(8.87, -1.48) * mm});
            skPoint(sketch, "E21.24.0", {"position": v(8.46, 0.39) * mm});
            skPoint(sketch, "E21.24.1", {"position": v(9, 0.28) * mm});
            skPoint(sketch, "E21.24.2", {"position": v(7.93, 0.39) * mm});
            skArc(sketch, "E21.24.3", {"start": v(7.93, -0.39) * mm, "mid": v(7.92, -0.58) * mm, "end": v(7.9, -0.78) * mm});
            skLineSegment(sketch, "E21.24.4", {"start": v(9, -0.28) * mm, "end": v(8.46, -0.39) * mm});
            skLineSegment(sketch, "E21.24.5", {"start": v(7.93, -0.39) * mm, "end": v(8.46, -0.39) * mm});
            skArc(sketch, "E21.24.6", {"start": v(7.93, 0.39) * mm, "mid": v(7.92, 0.58) * mm, "end": v(7.9, 0.78) * mm});
            skPoint(sketch, "E21.24.7", {"position": v(8.46, -0.39) * mm});
            skPoint(sketch, "E21.24.8", {"position": v(9, -0.28) * mm});
            skPoint(sketch, "E21.24.9", {"position": v(7.93, -0.39) * mm});
            skLineSegment(sketch, "E21.24.10", {"start": v(7.93, 0.39) * mm, "end": v(8.46, 0.39) * mm});
            skLineSegment(sketch, "E21.24.11", {"start": v(9, 0.28) * mm, "end": v(8.46, 0.39) * mm});
            skArc(sketch, "E21.24.12", {"start": v(9, 0) * mm, "mid": v(9, -0.14) * mm, "end": v(9, -0.28) * mm});
            skArc(sketch, "E21.24.13", {"start": v(9, 0) * mm, "mid": v(9, 0.14) * mm, "end": v(9, 0.28) * mm});
            skPoint(sketch, "E21.25.0", {"position": v(8.22, 2.03) * mm});
            skPoint(sketch, "E21.25.1", {"position": v(8.76, 2.02) * mm});
            skPoint(sketch, "E21.25.2", {"position": v(7.7, 1.93) * mm});
            skArc(sketch, "E21.25.3", {"start": v(7.85, 1.16) * mm, "mid": v(7.88, 0.97) * mm, "end": v(7.9, 0.78) * mm});
            skLineSegment(sketch, "E21.25.4", {"start": v(8.87, 1.48) * mm, "end": v(8.37, 1.27) * mm});
            skLineSegment(sketch, "E21.25.5", {"start": v(7.85, 1.16) * mm, "end": v(8.37, 1.27) * mm});
            skArc(sketch, "E21.25.6", {"start": v(7.7, 1.93) * mm, "mid": v(7.65, 2.12) * mm, "end": v(7.6, 2.3) * mm});
            skPoint(sketch, "E21.25.7", {"position": v(8.37, 1.27) * mm});
            skPoint(sketch, "E21.25.8", {"position": v(8.87, 1.48) * mm});
            skPoint(sketch, "E21.25.9", {"position": v(7.85, 1.16) * mm});
            skLineSegment(sketch, "E21.25.10", {"start": v(7.7, 1.93) * mm, "end": v(8.22, 2.03) * mm});
            skLineSegment(sketch, "E21.25.11", {"start": v(8.76, 2.02) * mm, "end": v(8.22, 2.03) * mm});
            skArc(sketch, "E21.25.12", {"start": v(8.82, 1.76) * mm, "mid": v(8.85, 1.62) * mm, "end": v(8.87, 1.48) * mm});
            skArc(sketch, "E21.25.13", {"start": v(8.82, 1.76) * mm, "mid": v(8.8, 1.9) * mm, "end": v(8.76, 2.02) * mm});
            skPoint(sketch, "E21.26.0", {"position": v(7.66, 3.6) * mm});
            skPoint(sketch, "E21.26.1", {"position": v(8.2, 3.7) * mm});
            skPoint(sketch, "E21.26.2", {"position": v(7.18, 3.4) * mm});
            skArc(sketch, "E21.26.3", {"start": v(7.47, 2.67) * mm, "mid": v(7.54, 2.49) * mm, "end": v(7.6, 2.3) * mm});
            skLineSegment(sketch, "E21.26.4", {"start": v(8.41, 3.19) * mm, "end": v(7.96, 2.88) * mm});
            skLineSegment(sketch, "E21.26.5", {"start": v(7.47, 2.67) * mm, "end": v(7.96, 2.88) * mm});
            skArc(sketch, "E21.26.6", {"start": v(7.18, 3.4) * mm, "mid": v(7.09, 3.57) * mm, "end": v(7, 3.74) * mm});
            skPoint(sketch, "E21.26.7", {"position": v(7.96, 2.88) * mm});
            skPoint(sketch, "E21.26.8", {"position": v(8.41, 3.19) * mm});
            skPoint(sketch, "E21.26.9", {"position": v(7.47, 2.67) * mm});
            skLineSegment(sketch, "E21.26.10", {"start": v(7.18, 3.4) * mm, "end": v(7.66, 3.6) * mm});
            skLineSegment(sketch, "E21.26.11", {"start": v(8.2, 3.7) * mm, "end": v(7.66, 3.6) * mm});
            skArc(sketch, "E21.26.12", {"start": v(8.31, 3.44) * mm, "mid": v(8.36, 3.31) * mm, "end": v(8.41, 3.19) * mm});
            skArc(sketch, "E21.26.13", {"start": v(8.31, 3.44) * mm, "mid": v(8.26, 3.57) * mm, "end": v(8.2, 3.7) * mm});
            skPoint(sketch, "E21.27.0", {"position": v(6.82, 5.02) * mm});
            skPoint(sketch, "E21.27.1", {"position": v(7.32, 5.22) * mm});
            skPoint(sketch, "E21.27.2", {"position": v(6.38, 4.73) * mm});
            skArc(sketch, "E21.27.3", {"start": v(6.8, 4.08) * mm, "mid": v(6.9, 3.91) * mm, "end": v(7, 3.74) * mm});
            skLineSegment(sketch, "E21.27.4", {"start": v(7.63, 4.77) * mm, "end": v(7.25, 4.37) * mm});
            skLineSegment(sketch, "E21.27.5", {"start": v(6.8, 4.08) * mm, "end": v(7.25, 4.37) * mm});
            skArc(sketch, "E21.27.6", {"start": v(6.38, 4.73) * mm, "mid": v(6.26, 4.88) * mm, "end": v(6.14, 5.04) * mm});
            skPoint(sketch, "E21.27.7", {"position": v(7.25, 4.37) * mm});
            skPoint(sketch, "E21.27.8", {"position": v(7.63, 4.77) * mm});
            skPoint(sketch, "E21.27.9", {"position": v(6.8, 4.08) * mm});
            skLineSegment(sketch, "E21.27.10", {"start": v(6.38, 4.73) * mm, "end": v(6.82, 5.02) * mm});
            skLineSegment(sketch, "E21.27.11", {"start": v(7.32, 5.22) * mm, "end": v(6.82, 5.02) * mm});
            skArc(sketch, "E21.27.12", {"start": v(7.48, 5) * mm, "mid": v(7.56, 4.88) * mm, "end": v(7.63, 4.77) * mm});
            skArc(sketch, "E21.27.13", {"start": v(7.48, 5) * mm, "mid": v(7.4, 5.11) * mm, "end": v(7.32, 5.22) * mm});
            skPoint(sketch, "E21.28.0", {"position": v(5.7, 6.26) * mm});
            skPoint(sketch, "E21.28.1", {"position": v(6.16, 6.55) * mm});
            skPoint(sketch, "E21.28.2", {"position": v(5.33, 5.88) * mm});
            skArc(sketch, "E21.28.3", {"start": v(5.88, 5.33) * mm, "mid": v(6.01, 5.18) * mm, "end": v(6.14, 5.04) * mm});
            skLineSegment(sketch, "E21.28.4", {"start": v(6.55, 6.16) * mm, "end": v(6.26, 5.7) * mm});
            skLineSegment(sketch, "E21.28.5", {"start": v(5.88, 5.33) * mm, "end": v(6.26, 5.7) * mm});
            skArc(sketch, "E21.28.6", {"start": v(5.33, 5.88) * mm, "mid": v(5.18, 6.01) * mm, "end": v(5.04, 6.14) * mm});
            skPoint(sketch, "E21.28.7", {"position": v(6.26, 5.7) * mm});
            skPoint(sketch, "E21.28.8", {"position": v(6.55, 6.16) * mm});
            skPoint(sketch, "E21.28.9", {"position": v(5.88, 5.33) * mm});
            skLineSegment(sketch, "E21.28.10", {"start": v(5.33, 5.88) * mm, "end": v(5.7, 6.26) * mm});
            skLineSegment(sketch, "E21.28.11", {"start": v(6.16, 6.55) * mm, "end": v(5.7, 6.26) * mm});
            skArc(sketch, "E21.28.12", {"start": v(6.36, 6.36) * mm, "mid": v(6.46, 6.26) * mm, "end": v(6.55, 6.16) * mm});
            skArc(sketch, "E21.28.13", {"start": v(6.36, 6.36) * mm, "mid": v(6.26, 6.46) * mm, "end": v(6.16, 6.55) * mm});
            skPoint(sketch, "E21.29.0", {"position": v(4.37, 7.25) * mm});
            skPoint(sketch, "E21.29.1", {"position": v(4.77, 7.63) * mm});
            skPoint(sketch, "E21.29.2", {"position": v(4.08, 6.8) * mm});
            skArc(sketch, "E21.29.3", {"start": v(4.73, 6.38) * mm, "mid": v(4.88, 6.26) * mm, "end": v(5.04, 6.14) * mm});
            skLineSegment(sketch, "E21.29.4", {"start": v(5.22, 7.32) * mm, "end": v(5.02, 6.82) * mm});
            skLineSegment(sketch, "E21.29.5", {"start": v(4.73, 6.38) * mm, "end": v(5.02, 6.82) * mm});
            skArc(sketch, "E21.29.6", {"start": v(4.08, 6.8) * mm, "mid": v(3.91, 6.9) * mm, "end": v(3.74, 7) * mm});
            skPoint(sketch, "E21.29.7", {"position": v(5.02, 6.82) * mm});
            skPoint(sketch, "E21.29.8", {"position": v(5.22, 7.32) * mm});
            skPoint(sketch, "E21.29.9", {"position": v(4.73, 6.38) * mm});
            skLineSegment(sketch, "E21.29.10", {"start": v(4.08, 6.8) * mm, "end": v(4.37, 7.25) * mm});
            skLineSegment(sketch, "E21.29.11", {"start": v(4.77, 7.63) * mm, "end": v(4.37, 7.25) * mm});
            skArc(sketch, "E21.29.12", {"start": v(5, 7.48) * mm, "mid": v(5.11, 7.4) * mm, "end": v(5.22, 7.32) * mm});
            skArc(sketch, "E21.29.13", {"start": v(5, 7.48) * mm, "mid": v(4.88, 7.56) * mm, "end": v(4.77, 7.63) * mm});
            skPoint(sketch, "E21.30.0", {"position": v(2.88, 7.96) * mm});
            skPoint(sketch, "E21.30.1", {"position": v(3.19, 8.41) * mm});
            skPoint(sketch, "E21.30.2", {"position": v(2.67, 7.47) * mm});
            skArc(sketch, "E21.30.3", {"start": v(3.4, 7.18) * mm, "mid": v(3.57, 7.09) * mm, "end": v(3.74, 7) * mm});
            skLineSegment(sketch, "E21.30.4", {"start": v(3.7, 8.2) * mm, "end": v(3.6, 7.66) * mm});
            skLineSegment(sketch, "E21.30.5", {"start": v(3.4, 7.18) * mm, "end": v(3.6, 7.66) * mm});
            skArc(sketch, "E21.30.6", {"start": v(2.67, 7.47) * mm, "mid": v(2.49, 7.54) * mm, "end": v(2.3, 7.6) * mm});
            skPoint(sketch, "E21.30.7", {"position": v(3.6, 7.66) * mm});
            skPoint(sketch, "E21.30.8", {"position": v(3.7, 8.2) * mm});
            skPoint(sketch, "E21.30.9", {"position": v(3.4, 7.18) * mm});
            skLineSegment(sketch, "E21.30.10", {"start": v(2.67, 7.47) * mm, "end": v(2.88, 7.96) * mm});
            skLineSegment(sketch, "E21.30.11", {"start": v(3.19, 8.41) * mm, "end": v(2.88, 7.96) * mm});
            skArc(sketch, "E21.30.12", {"start": v(3.44, 8.31) * mm, "mid": v(3.57, 8.26) * mm, "end": v(3.7, 8.2) * mm});
            skArc(sketch, "E21.30.13", {"start": v(3.44, 8.31) * mm, "mid": v(3.31, 8.36) * mm, "end": v(3.19, 8.41) * mm});
            skPoint(sketch, "E21.31.0", {"position": v(1.27, 8.37) * mm});
            skPoint(sketch, "E21.31.1", {"position": v(1.48, 8.87) * mm});
            skPoint(sketch, "E21.31.2", {"position": v(1.16, 7.85) * mm});
            skArc(sketch, "E21.31.3", {"start": v(1.93, 7.7) * mm, "mid": v(2.12, 7.65) * mm, "end": v(2.3, 7.6) * mm});
            skLineSegment(sketch, "E21.31.4", {"start": v(2.02, 8.76) * mm, "end": v(2.03, 8.22) * mm});
            skLineSegment(sketch, "E21.31.5", {"start": v(1.93, 7.7) * mm, "end": v(2.03, 8.22) * mm});
            skArc(sketch, "E21.31.6", {"start": v(1.16, 7.85) * mm, "mid": v(0.97, 7.88) * mm, "end": v(0.78, 7.9) * mm});
            skPoint(sketch, "E21.31.7", {"position": v(2.03, 8.22) * mm});
            skPoint(sketch, "E21.31.8", {"position": v(2.02, 8.76) * mm});
            skPoint(sketch, "E21.31.9", {"position": v(1.93, 7.7) * mm});
            skLineSegment(sketch, "E21.31.10", {"start": v(1.16, 7.85) * mm, "end": v(1.27, 8.37) * mm});
            skLineSegment(sketch, "E21.31.11", {"start": v(1.48, 8.87) * mm, "end": v(1.27, 8.37) * mm});
            skArc(sketch, "E21.31.12", {"start": v(1.76, 8.82) * mm, "mid": v(1.9, 8.8) * mm, "end": v(2.02, 8.76) * mm});
            skArc(sketch, "E21.31.13", {"start": v(1.76, 8.82) * mm, "mid": v(1.62, 8.85) * mm, "end": v(1.48, 8.87) * mm});
            skSolve(sketch);
        }
        {
            var Q0;
            {var subQ0=sQuery(id+"F0.wireOp",EDGE,"E21.25.4");Q0=makeQuery(id+"F0.imprint","IMPRINT",FACE,{"disambiguationData":[TD([[makeQuery(id+"F0.imprint","IMPRINT",EDGE,{"derivedFrom":subQ0}),-1.0]])]});}
            var Q1;
            {var subQ0=sQuery(id+"F0.wireOp",EDGE,"E21.26.4");Q1=makeQuery(id+"F0.imprint","IMPRINT",FACE,{"disambiguationData":[TD([[makeQuery(id+"F0.imprint","IMPRINT",EDGE,{"derivedFrom":subQ0}),-1.0]])]});}
            var Q2;
            {var subQ0=sQuery(id+"F0.wireOp",EDGE,"E21.27.4");Q2=makeQuery(id+"F0.imprint","IMPRINT",FACE,{"disambiguationData":[TD([[makeQuery(id+"F0.imprint","IMPRINT",EDGE,{"derivedFrom":subQ0}),-1.0]])]});}
            var Q3;
            {var subQ0=sQuery(id+"F0.wireOp",EDGE,"E21.28.4");Q3=makeQuery(id+"F0.imprint","IMPRINT",FACE,{"disambiguationData":[TD([[makeQuery(id+"F0.imprint","IMPRINT",EDGE,{"derivedFrom":subQ0}),-1.0]])]});}
            var Q4;
            {var subQ0=sQuery(id+"F0.wireOp",EDGE,"E21.29.4");Q4=makeQuery(id+"F0.imprint","IMPRINT",FACE,{"disambiguationData":[TD([[makeQuery(id+"F0.imprint","IMPRINT",EDGE,{"derivedFrom":subQ0}),-1.0]])]});}
            var Q5;
            {var subQ0=sQuery(id+"F0.wireOp",EDGE,"E21.30.4");Q5=makeQuery(id+"F0.imprint","IMPRINT",FACE,{"disambiguationData":[TD([[makeQuery(id+"F0.imprint","IMPRINT",EDGE,{"derivedFrom":subQ0}),-1.0]])]});}
            var Q6;
            {var subQ0=sQuery(id+"F0.wireOp",EDGE,"E21.31.4");Q6=makeQuery(id+"F0.imprint","IMPRINT",FACE,{"disambiguationData":[TD([[makeQuery(id+"F0.imprint","IMPRINT",EDGE,{"derivedFrom":subQ0}),-1.0]])]});}
            var Q7;
            {var subQ0=sQuery(id+"F0.wireOp",EDGE,"E12");Q7=makeQuery(id+"F0.imprint","IMPRINT",FACE,{"disambiguationData":[TD([[makeQuery(id+"F0.imprint","IMPRINT",EDGE,{"derivedFrom":subQ0}),-1.0]])]});}
            var Q8;
            {var subQ0=sQuery(id+"F0.wireOp",EDGE,"E20.MirrorCS");Q8=makeQuery(id+"F0.imprint","IMPRINT",FACE,{"disambiguationData":[TD([[makeQuery(id+"F0.imprint","IMPRINT",EDGE,{"derivedFrom":subQ0}),1.0]])]});}
            var Q9;
            {var subQ0=sQuery(id+"F0.wireOp",EDGE,"E21.1.4");Q9=makeQuery(id+"F0.imprint","IMPRINT",FACE,{"disambiguationData":[TD([[makeQuery(id+"F0.imprint","IMPRINT",EDGE,{"derivedFrom":subQ0}),-1.0]])]});}
            var Q10;
            {var subQ0=sQuery(id+"F0.wireOp",EDGE,"E21.2.4");Q10=makeQuery(id+"F0.imprint","IMPRINT",FACE,{"disambiguationData":[TD([[makeQuery(id+"F0.imprint","IMPRINT",EDGE,{"derivedFrom":subQ0}),-1.0]])]});}
            var Q11;
            {var subQ0=sQuery(id+"F0.wireOp",EDGE,"E21.3.4");Q11=makeQuery(id+"F0.imprint","IMPRINT",FACE,{"disambiguationData":[TD([[makeQuery(id+"F0.imprint","IMPRINT",EDGE,{"derivedFrom":subQ0}),-1.0]])]});}
            var Q12;
            {var subQ0=sQuery(id+"F0.wireOp",EDGE,"E21.4.4");Q12=makeQuery(id+"F0.imprint","IMPRINT",FACE,{"disambiguationData":[TD([[makeQuery(id+"F0.imprint","IMPRINT",EDGE,{"derivedFrom":subQ0}),-1.0]])]});}
            var Q13;
            {var subQ0=sQuery(id+"F0.wireOp",EDGE,"E21.5.4");Q13=makeQuery(id+"F0.imprint","IMPRINT",FACE,{"disambiguationData":[TD([[makeQuery(id+"F0.imprint","IMPRINT",EDGE,{"derivedFrom":subQ0}),-1.0]])]});}
            var Q14;
            {var subQ0=sQuery(id+"F0.wireOp",EDGE,"E21.6.4");Q14=makeQuery(id+"F0.imprint","IMPRINT",FACE,{"disambiguationData":[TD([[makeQuery(id+"F0.imprint","IMPRINT",EDGE,{"derivedFrom":subQ0}),-1.0]])]});}
            var Q15;
            {var subQ0=sQuery(id+"F0.wireOp",EDGE,"E21.7.4");Q15=makeQuery(id+"F0.imprint","IMPRINT",FACE,{"disambiguationData":[TD([[makeQuery(id+"F0.imprint","IMPRINT",EDGE,{"derivedFrom":subQ0}),-1.0]])]});}
            var Q16;
            {var subQ0=sQuery(id+"F0.wireOp",EDGE,"E21.8.4");Q16=makeQuery(id+"F0.imprint","IMPRINT",FACE,{"disambiguationData":[TD([[makeQuery(id+"F0.imprint","IMPRINT",EDGE,{"derivedFrom":subQ0}),-1.0]])]});}
            var Q17;
            {var subQ0=sQuery(id+"F0.wireOp",EDGE,"E21.9.4");Q17=makeQuery(id+"F0.imprint","IMPRINT",FACE,{"disambiguationData":[TD([[makeQuery(id+"F0.imprint","IMPRINT",EDGE,{"derivedFrom":subQ0}),-1.0]])]});}
            var Q18;
            {var subQ0=sQuery(id+"F0.wireOp",EDGE,"E21.10.4");Q18=makeQuery(id+"F0.imprint","IMPRINT",FACE,{"disambiguationData":[TD([[makeQuery(id+"F0.imprint","IMPRINT",EDGE,{"derivedFrom":subQ0}),-1.0]])]});}
            var Q19;
            {var subQ0=sQuery(id+"F0.wireOp",EDGE,"E21.11.4");Q19=makeQuery(id+"F0.imprint","IMPRINT",FACE,{"disambiguationData":[TD([[makeQuery(id+"F0.imprint","IMPRINT",EDGE,{"derivedFrom":subQ0}),-1.0]])]});}
            var Q20;
            {var subQ0=sQuery(id+"F0.wireOp",EDGE,"E21.12.4");Q20=makeQuery(id+"F0.imprint","IMPRINT",FACE,{"disambiguationData":[TD([[makeQuery(id+"F0.imprint","IMPRINT",EDGE,{"derivedFrom":subQ0}),-1.0]])]});}
            var Q21;
            {var subQ0=sQuery(id+"F0.wireOp",EDGE,"E21.13.4");Q21=makeQuery(id+"F0.imprint","IMPRINT",FACE,{"disambiguationData":[TD([[makeQuery(id+"F0.imprint","IMPRINT",EDGE,{"derivedFrom":subQ0}),-1.0]])]});}
            var Q22;
            {var subQ0=sQuery(id+"F0.wireOp",EDGE,"E21.14.4");Q22=makeQuery(id+"F0.imprint","IMPRINT",FACE,{"disambiguationData":[TD([[makeQuery(id+"F0.imprint","IMPRINT",EDGE,{"derivedFrom":subQ0}),-1.0]])]});}
            var Q23;
            {var subQ0=sQuery(id+"F0.wireOp",EDGE,"E21.15.4");Q23=makeQuery(id+"F0.imprint","IMPRINT",FACE,{"disambiguationData":[TD([[makeQuery(id+"F0.imprint","IMPRINT",EDGE,{"derivedFrom":subQ0}),-1.0]])]});}
            var Q24;
            {var subQ0=sQuery(id+"F0.wireOp",EDGE,"E21.16.4");Q24=makeQuery(id+"F0.imprint","IMPRINT",FACE,{"disambiguationData":[TD([[makeQuery(id+"F0.imprint","IMPRINT",EDGE,{"derivedFrom":subQ0}),-1.0]])]});}
            var Q25;
            {var subQ0=sQuery(id+"F0.wireOp",EDGE,"E21.17.4");Q25=makeQuery(id+"F0.imprint","IMPRINT",FACE,{"disambiguationData":[TD([[makeQuery(id+"F0.imprint","IMPRINT",EDGE,{"derivedFrom":subQ0}),-1.0]])]});}
            var Q26;
            {var subQ0=sQuery(id+"F0.wireOp",EDGE,"E21.18.4");Q26=makeQuery(id+"F0.imprint","IMPRINT",FACE,{"disambiguationData":[TD([[makeQuery(id+"F0.imprint","IMPRINT",EDGE,{"derivedFrom":subQ0}),-1.0]])]});}
            var Q27;
            {var subQ0=sQuery(id+"F0.wireOp",EDGE,"E21.19.4");Q27=makeQuery(id+"F0.imprint","IMPRINT",FACE,{"disambiguationData":[TD([[makeQuery(id+"F0.imprint","IMPRINT",EDGE,{"derivedFrom":subQ0}),-1.0]])]});}
            var Q28;
            {var subQ0=sQuery(id+"F0.wireOp",EDGE,"E21.20.4");Q28=makeQuery(id+"F0.imprint","IMPRINT",FACE,{"disambiguationData":[TD([[makeQuery(id+"F0.imprint","IMPRINT",EDGE,{"derivedFrom":subQ0}),-1.0]])]});}
            var Q29;
            {var subQ0=sQuery(id+"F0.wireOp",EDGE,"E21.21.4");Q29=makeQuery(id+"F0.imprint","IMPRINT",FACE,{"disambiguationData":[TD([[makeQuery(id+"F0.imprint","IMPRINT",EDGE,{"derivedFrom":subQ0}),-1.0]])]});}
            var Q30;
            {var subQ0=sQuery(id+"F0.wireOp",EDGE,"E21.22.4");Q30=makeQuery(id+"F0.imprint","IMPRINT",FACE,{"disambiguationData":[TD([[makeQuery(id+"F0.imprint","IMPRINT",EDGE,{"derivedFrom":subQ0}),-1.0]])]});}
            var Q31;
            {var subQ0=sQuery(id+"F0.wireOp",EDGE,"E21.23.4");Q31=makeQuery(id+"F0.imprint","IMPRINT",FACE,{"disambiguationData":[TD([[makeQuery(id+"F0.imprint","IMPRINT",EDGE,{"derivedFrom":subQ0}),-1.0]])]});}
            var Q32;
            {var subQ0=sQuery(id+"F0.wireOp",EDGE,"E21.24.4");Q32=makeQuery(id+"F0.imprint","IMPRINT",FACE,{"disambiguationData":[TD([[makeQuery(id+"F0.imprint","IMPRINT",EDGE,{"derivedFrom":subQ0}),-1.0]])]});}
            var Q33;
            {var subQ0=sQuery(id+"F0.wireOp",EDGE,"E21.13.5");Q33=makeQuery(id+"F0.imprint","IMPRINT",FACE,{"disambiguationData":[TD([[makeQuery(id+"F0.imprint","IMPRINT",EDGE,{"derivedFrom":subQ0}),1.0]])]});}
            var Q34;
            {var subQ0=sQuery(id+"F0.wireOp",EDGE,"E21.14.5");Q34=makeQuery(id+"F0.imprint","IMPRINT",FACE,{"disambiguationData":[TD([[makeQuery(id+"F0.imprint","IMPRINT",EDGE,{"derivedFrom":subQ0}),1.0]])]});}
            var Q35;
            {var subQ0=sQuery(id+"F0.wireOp",EDGE,"E21.15.5");Q35=makeQuery(id+"F0.imprint","IMPRINT",FACE,{"disambiguationData":[TD([[makeQuery(id+"F0.imprint","IMPRINT",EDGE,{"derivedFrom":subQ0}),1.0]])]});}
            var Q36;
            {var subQ0=sQuery(id+"F0.wireOp",EDGE,"E21.16.5");Q36=makeQuery(id+"F0.imprint","IMPRINT",FACE,{"disambiguationData":[TD([[makeQuery(id+"F0.imprint","IMPRINT",EDGE,{"derivedFrom":subQ0}),1.0]])]});}
            var Q37;
            {var subQ0=sQuery(id+"F0.wireOp",EDGE,"E21.17.5");Q37=makeQuery(id+"F0.imprint","IMPRINT",FACE,{"disambiguationData":[TD([[makeQuery(id+"F0.imprint","IMPRINT",EDGE,{"derivedFrom":subQ0}),1.0]])]});}
            var Q38;
            {var subQ0=sQuery(id+"F0.wireOp",EDGE,"E21.18.5");Q38=makeQuery(id+"F0.imprint","IMPRINT",FACE,{"disambiguationData":[TD([[makeQuery(id+"F0.imprint","IMPRINT",EDGE,{"derivedFrom":subQ0}),1.0]])]});}
            var Q39;
            {var subQ0=sQuery(id+"F0.wireOp",EDGE,"E21.19.5");Q39=makeQuery(id+"F0.imprint","IMPRINT",FACE,{"disambiguationData":[TD([[makeQuery(id+"F0.imprint","IMPRINT",EDGE,{"derivedFrom":subQ0}),1.0]])]});}
            var Q40;
            {var subQ0=sQuery(id+"F0.wireOp",EDGE,"E21.20.5");Q40=makeQuery(id+"F0.imprint","IMPRINT",FACE,{"disambiguationData":[TD([[makeQuery(id+"F0.imprint","IMPRINT",EDGE,{"derivedFrom":subQ0}),1.0]])]});}
            var Q41;
            {var subQ0=sQuery(id+"F0.wireOp",EDGE,"E21.21.5");Q41=makeQuery(id+"F0.imprint","IMPRINT",FACE,{"disambiguationData":[TD([[makeQuery(id+"F0.imprint","IMPRINT",EDGE,{"derivedFrom":subQ0}),1.0]])]});}
            var Q42;
            {var subQ0=sQuery(id+"F0.wireOp",EDGE,"E21.22.5");Q42=makeQuery(id+"F0.imprint","IMPRINT",FACE,{"disambiguationData":[TD([[makeQuery(id+"F0.imprint","IMPRINT",EDGE,{"derivedFrom":subQ0}),1.0]])]});}
            var Q43;
            {var subQ0=sQuery(id+"F0.wireOp",EDGE,"E21.23.5");Q43=makeQuery(id+"F0.imprint","IMPRINT",FACE,{"disambiguationData":[TD([[makeQuery(id+"F0.imprint","IMPRINT",EDGE,{"derivedFrom":subQ0}),1.0]])]});}
            var Q44;
            {var subQ0=sQuery(id+"F0.wireOp",EDGE,"E21.24.5");Q44=makeQuery(id+"F0.imprint","IMPRINT",FACE,{"disambiguationData":[TD([[makeQuery(id+"F0.imprint","IMPRINT",EDGE,{"derivedFrom":subQ0}),1.0]])]});}
            var Q45;
            {var subQ0=sQuery(id+"F0.wireOp",EDGE,"E21.25.5");Q45=makeQuery(id+"F0.imprint","IMPRINT",FACE,{"disambiguationData":[TD([[makeQuery(id+"F0.imprint","IMPRINT",EDGE,{"derivedFrom":subQ0}),1.0]])]});}
            var Q46;
            {var subQ0=sQuery(id+"F0.wireOp",EDGE,"E21.26.5");Q46=makeQuery(id+"F0.imprint","IMPRINT",FACE,{"disambiguationData":[TD([[makeQuery(id+"F0.imprint","IMPRINT",EDGE,{"derivedFrom":subQ0}),1.0]])]});}
            var Q47;
            {var subQ0=sQuery(id+"F0.wireOp",EDGE,"E21.27.5");Q47=makeQuery(id+"F0.imprint","IMPRINT",FACE,{"disambiguationData":[TD([[makeQuery(id+"F0.imprint","IMPRINT",EDGE,{"derivedFrom":subQ0}),1.0]])]});}
            var Q48;
            {var subQ0=sQuery(id+"F0.wireOp",EDGE,"E21.28.5");Q48=makeQuery(id+"F0.imprint","IMPRINT",FACE,{"disambiguationData":[TD([[makeQuery(id+"F0.imprint","IMPRINT",EDGE,{"derivedFrom":subQ0}),1.0]])]});}
            var Q49;
            {var subQ0=sQuery(id+"F0.wireOp",EDGE,"E21.29.5");Q49=makeQuery(id+"F0.imprint","IMPRINT",FACE,{"disambiguationData":[TD([[makeQuery(id+"F0.imprint","IMPRINT",EDGE,{"derivedFrom":subQ0}),1.0]])]});}
            var Q50;
            {var subQ0=sQuery(id+"F0.wireOp",EDGE,"E21.30.5");Q50=makeQuery(id+"F0.imprint","IMPRINT",FACE,{"disambiguationData":[TD([[makeQuery(id+"F0.imprint","IMPRINT",EDGE,{"derivedFrom":subQ0}),1.0]])]});}
            var Q51;
            {var subQ0=sQuery(id+"F0.wireOp",EDGE,"E21.31.5");Q51=makeQuery(id+"F0.imprint","IMPRINT",FACE,{"disambiguationData":[TD([[makeQuery(id+"F0.imprint","IMPRINT",EDGE,{"derivedFrom":subQ0}),1.0]])]});}
            var Q52;
            {var subQ0=sQuery(id+"F0.wireOp",EDGE,"E13");Q52=makeQuery(id+"F0.imprint","IMPRINT",FACE,{"disambiguationData":[TD([[makeQuery(id+"F0.imprint","IMPRINT",EDGE,{"derivedFrom":subQ0}),1.0]])]});}
            var Q53;
            {var subQ0=sQuery(id+"F0.wireOp",EDGE,"E21.1.5");Q53=makeQuery(id+"F0.imprint","IMPRINT",FACE,{"disambiguationData":[TD([[makeQuery(id+"F0.imprint","IMPRINT",EDGE,{"derivedFrom":subQ0}),1.0]])]});}
            var Q54;
            {var subQ0=sQuery(id+"F0.wireOp",EDGE,"E21.2.5");Q54=makeQuery(id+"F0.imprint","IMPRINT",FACE,{"disambiguationData":[TD([[makeQuery(id+"F0.imprint","IMPRINT",EDGE,{"derivedFrom":subQ0}),1.0]])]});}
            var Q55;
            {var subQ0=sQuery(id+"F0.wireOp",EDGE,"E21.3.5");Q55=makeQuery(id+"F0.imprint","IMPRINT",FACE,{"disambiguationData":[TD([[makeQuery(id+"F0.imprint","IMPRINT",EDGE,{"derivedFrom":subQ0}),1.0]])]});}
            var Q56;
            {var subQ0=sQuery(id+"F0.wireOp",EDGE,"E21.4.5");Q56=makeQuery(id+"F0.imprint","IMPRINT",FACE,{"disambiguationData":[TD([[makeQuery(id+"F0.imprint","IMPRINT",EDGE,{"derivedFrom":subQ0}),1.0]])]});}
            var Q57;
            {var subQ0=sQuery(id+"F0.wireOp",EDGE,"E21.5.5");Q57=makeQuery(id+"F0.imprint","IMPRINT",FACE,{"disambiguationData":[TD([[makeQuery(id+"F0.imprint","IMPRINT",EDGE,{"derivedFrom":subQ0}),1.0]])]});}
            var Q58;
            {var subQ0=sQuery(id+"F0.wireOp",EDGE,"E21.6.5");Q58=makeQuery(id+"F0.imprint","IMPRINT",FACE,{"disambiguationData":[TD([[makeQuery(id+"F0.imprint","IMPRINT",EDGE,{"derivedFrom":subQ0}),1.0]])]});}
            var Q59;
            {var subQ0=sQuery(id+"F0.wireOp",EDGE,"E21.7.5");Q59=makeQuery(id+"F0.imprint","IMPRINT",FACE,{"disambiguationData":[TD([[makeQuery(id+"F0.imprint","IMPRINT",EDGE,{"derivedFrom":subQ0}),1.0]])]});}
            var Q60;
            {var subQ0=sQuery(id+"F0.wireOp",EDGE,"E21.8.5");Q60=makeQuery(id+"F0.imprint","IMPRINT",FACE,{"disambiguationData":[TD([[makeQuery(id+"F0.imprint","IMPRINT",EDGE,{"derivedFrom":subQ0}),1.0]])]});}
            var Q61;
            {var subQ0=sQuery(id+"F0.wireOp",EDGE,"E21.9.5");Q61=makeQuery(id+"F0.imprint","IMPRINT",FACE,{"disambiguationData":[TD([[makeQuery(id+"F0.imprint","IMPRINT",EDGE,{"derivedFrom":subQ0}),1.0]])]});}
            var Q62;
            {var subQ0=sQuery(id+"F0.wireOp",EDGE,"E21.10.5");Q62=makeQuery(id+"F0.imprint","IMPRINT",FACE,{"disambiguationData":[TD([[makeQuery(id+"F0.imprint","IMPRINT",EDGE,{"derivedFrom":subQ0}),1.0]])]});}
            var Q63;
            {var subQ0=sQuery(id+"F0.wireOp",EDGE,"E21.11.5");Q63=makeQuery(id+"F0.imprint","IMPRINT",FACE,{"disambiguationData":[TD([[makeQuery(id+"F0.imprint","IMPRINT",EDGE,{"derivedFrom":subQ0}),1.0]])]});}
            var Q64;
            {var subQ0=sQuery(id+"F0.wireOp",EDGE,"E21.12.5");Q64=makeQuery(id+"F0.imprint","IMPRINT",FACE,{"disambiguationData":[TD([[makeQuery(id+"F0.imprint","IMPRINT",EDGE,{"derivedFrom":subQ0}),1.0]])]});}
            var Q65;
            {var subQ31=sQuery(id+"F0.wireOp",EDGE,"E5");var subQ32=sQuery(id+"F0.wireOp",EDGE,"E1.0");var subQ33=makeQuery(id+"F0.imprint","INTERSECT",VERTEX,{"derivedFrom":[subQ32,subQ31]});Q65=makeQuery(id+"F0.imprint","IMPRINT",FACE,{"disambiguationData":[TD([[makeQuery(id+"F0.imprint","IMPRINT",EDGE,{"disambiguationData":[TD([[subQ33,-1.0]])],"derivedFrom":subQ32}),-1.0]])]});}
            var Q66;
            {var subQ0=sQuery(id+"F0.wireOp",EDGE,"E19.MirrorCS");Q66=makeQuery(id+"F0.imprint","IMPRINT",FACE,{"disambiguationData":[TD([[makeQuery(id+"F0.imprint","IMPRINT",EDGE,{"derivedFrom":subQ0}),-1.0]])]});}
            var Q67;
            {var subQ0=sQuery(id+"F0.wireOp",EDGE,"E5");var subQ1=sQuery(id+"F0.wireOp",EDGE,"E1.0");var subQ2=makeQuery(id+"F0.imprint","INTERSECT",VERTEX,{"derivedFrom":[subQ1,subQ0]});Q67=makeQuery(id+"F0.imprint","IMPRINT",FACE,{"disambiguationData":[TD([[makeQuery(id+"F0.imprint","IMPRINT",EDGE,{"disambiguationData":[TD([[subQ2,1.0]])],"derivedFrom":subQ1}),-1.0]])]});}
            extrude(context, id + "F1", {"entities" : qUnion([Q0, Q1, Q2, Q3, Q4, Q5, Q6, Q7, Q8, Q9, Q10, Q11, Q12, Q13, Q14, Q15, Q16, Q17, Q18, Q19, Q20, Q21, Q22, Q23, Q24, Q25, Q26, Q27, Q28, Q29, Q30, Q31, Q32, Q33, Q34, Q35, Q36, Q37, Q38, Q39, Q40, Q41, Q42, Q43, Q44, Q45, Q46, Q47, Q48, Q49, Q50, Q51, Q52, Q53, Q54, Q55, Q56, Q57, Q58, Q59, Q60, Q61, Q62, Q63, Q64, Q65, Q66, Q67]), "depth" : .1 * mm, "offsetDistance" : 25.4 * mm});
        }
    });
